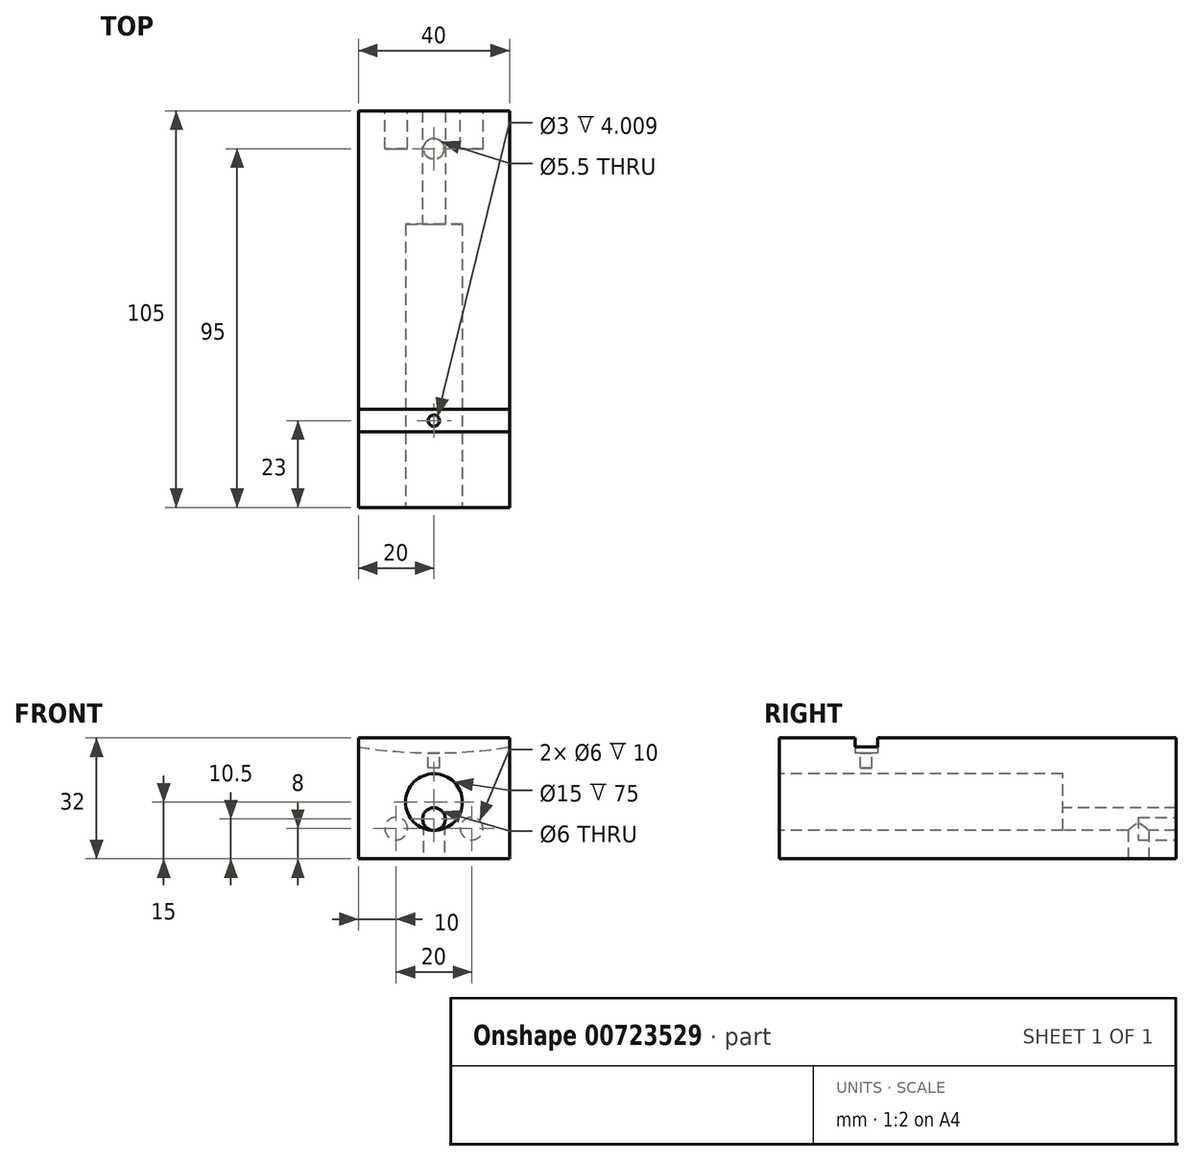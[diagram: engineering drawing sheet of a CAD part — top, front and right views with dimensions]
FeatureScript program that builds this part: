
annotation { "Feature Type Name" : "Feature", "Feature Type Description" : "" }
export const myFeature = defineFeature(function(context is Context, id is Id, definition is map)
    precondition{}
    {
        {
            var Q0;
            Q0=qCreatedBy(makeId("Front.planeOp"),FACE);
            var sketch = newSketch(context, id + "F0", { "sketchPlane" : qUnion([Q0])});
            skLineSegment(sketch, "E0.bottom", {"start": v(0, 0) * mm, "end": v(-40, 0) * mm});
            skLineSegment(sketch, "E0.top", {"start": v(0, 32) * mm, "end": v(-40, 32) * mm});
            skLineSegment(sketch, "E0.left", {"start": v(0, 0) * mm, "end": v(0, 32) * mm});
            skLineSegment(sketch, "E0.right", {"start": v(-40, 0) * mm, "end": v(-40, 32) * mm});
            skSolve(sketch);
        }
        {
            var Q0;
            Q0=qSketchRegion(id+"F0",true);
            extrude(context, id + "F1", {"entities" : qUnion([Q0]), "oppositeDirection" : true, "depth" : 105 * mm, "offsetDistance" : 25 * mm});
        }
        {
            var Q0;
            Q0=makeQuery(id+"F1.opExtrude","CAP_FACE",FACE,{"disambiguationData":[OSD([sQuery(id+"F0.wireOp",EDGE,"E0.bottom"),sQuery(id+"F0.wireOp",EDGE,"E0.top"),sQuery(id+"F0.wireOp",EDGE,"E0.left"),sQuery(id+"F0.wireOp",EDGE,"E0.right")])],"isStart":true});
            var sketch = newSketch(context, id + "F2", { "sketchPlane" : qUnion([Q0])});
            skPoint(sketch, "E1.centerSnap0", {"position": v(0, 16) * mm});
            skPoint(sketch, "E1.centerSnap1", {"position": v(-20, 0) * mm});
            skLineSegment(sketch, "E2", {"start": v(-20, 0) * mm, "end": v(-20, 15) * mm, "construction": true});
            skCircle(sketch, "E3", {"center": v(-20, 15) * mm, "radius": 7.5 * mm});
            skSolve(sketch);
        }
        {
            var Q0;
            Q0=qSketchRegion(id+"F2",true);
            extrude(context, id + "F3", {"entities" : qUnion([Q0]), "operationType" : NewBodyOperationType.REMOVE, "oppositeDirection" : true, "depth" : 75 * mm, "offsetDistance" : 25 * mm});
        }
        {
            var Q0;
            Q0=qCreatedBy(makeId("Front.planeOp"),FACE);
            var sketch = newSketch(context, id + "F4", { "sketchPlane" : qUnion([Q0])});
            skLineSegment(sketch, "E4", {"start": v(0, 0) * mm, "end": v(-20, 0) * mm, "construction": true});
            skLineSegment(sketch, "E5", {"start": v(-20, 0) * mm, "end": v(-20, 15) * mm, "construction": true});
            skLineSegment(sketch, "E6", {"start": v(-20, 15) * mm, "end": v(-20, 7.5) * mm, "construction": true});
            skLineSegment(sketch, "E7", {"start": v(-20, 7.5) * mm, "end": v(-20, 10.5) * mm, "construction": true});
            skCircle(sketch, "E8", {"center": v(-20, 10.5) * mm, "radius": 3 * mm});
            skSolve(sketch);
        }
        {
            var Q0;
            Q0=qSketchRegion(id+"F4",true);
            extrude(context, id + "F5", {"entities" : qUnion([Q0]), "operationType" : NewBodyOperationType.REMOVE, "endBound" : BoundingType.THROUGH_ALL, "oppositeDirection" : true, "depth" : 25 * mm, "offsetDistance" : 25 * mm});
        }
        {
            var Q0;
            Q0=qCreatedBy(makeId("Front.planeOp"),FACE);
            cPlane(context, id + "F6", {"entities" : qUnion([Q0]), "cplaneType" : CPlaneType.OFFSET, "offset" : 20 * mm, "oppositeDirection" : true, "width" : 150 * mm, "height" : 150 * mm});
        }
        {
            var Q0;
            Q0=qCreatedBy(id+"F6.planeOp",FACE);
            var sketch = newSketch(context, id + "F7", { "sketchPlane" : qUnion([Q0])});
            skLineSegment(sketch, "E9", {"start": v(0, 0) * mm, "end": v(0, 32) * mm, "construction": true});
            skLineSegment(sketch, "E10", {"start": v(0, 32) * mm, "end": v(-40, 32) * mm, "construction": true});
            skLineSegment(sketch, "E11", {"start": v(-40, 32) * mm, "end": v(-40, 28) * mm, "construction": true});
            skLineSegment(sketch, "E12", {"start": v(-40, 28) * mm, "end": v(0, 28) * mm, "construction": true});
            skLineSegment(sketch, "E13", {"start": v(-20, 28) * mm, "end": v(-20, 278) * mm, "construction": true});
            skCircle(sketch, "E14", {"center": v(-20, 153) * mm, "radius": 125 * mm});
            skLineSegment(sketch, "E15", {"start": v(0, 0) * mm, "end": v(-20, 0) * mm, "construction": true});
            skLineSegment(sketch, "E16", {"start": v(-20, 0) * mm, "end": v(-20, 22.5) * mm, "construction": true});
            skSolve(sketch);
        }
        {
            var Q0;
            Q0=qSketchRegion(id+"F7",true);
            extrude(context, id + "F8", {"entities" : qUnion([Q0]), "operationType" : NewBodyOperationType.REMOVE, "oppositeDirection" : true, "depth" : 6 * mm, "offsetDistance" : 25 * mm});
        }
        {
            var Q0;
            {var subQ2=sQuery(id+"F0.wireOp",EDGE,"E0.top");Q0=makeQuery(id+"F8.boolean.opBoolean","SPLIT",FACE,{"disambiguationData":[TD([makeQuery(id+"F8.opExtrude","CAP_FACE",FACE,{"disambiguationData":[OSD([sQuery(id+"F7.wireOp",EDGE,"E14")])],"isStart":false})])],"derivedFrom":makeQuery(id+"F1.opExtrude","SWEPT_FACE",FACE,{"disambiguationData":[OSD([subQ2])]})});}
            cPlane(context, id + "F9", {"entities" : qUnion([Q0]), "cplaneType" : CPlaneType.OFFSET, "offset" : 0 * mm, "width" : 150 * mm, "height" : 150 * mm});
        }
        {
            var Q0;
            Q0=qCreatedBy(id+"F9.planeOp",FACE);
            var sketch = newSketch(context, id + "F10", { "sketchPlane" : qUnion([Q0])});
            skLineSegment(sketch, "E17", {"start": v(0, 0) * mm, "end": v(0, 23) * mm, "construction": true});
            skLineSegment(sketch, "E18", {"start": v(0, 23) * mm, "end": v(-20, 23) * mm, "construction": true});
            skCircle(sketch, "E19", {"center": v(-20, 23) * mm, "radius": 1.5 * mm});
            skSolve(sketch);
        }
        {
            var Q0;
            Q0 = qSketchRegion(id + "F10", true);
            extrude(context, id + "F11", {"entities" : qUnion([Q0]), "operationType" : NewBodyOperationType.REMOVE, "oppositeDirection" : true, "depth" : 8 * mm, "offsetDistance" : 25 * mm});
        }
        {
            var Q0;
            Q0=makeQuery(id+"F1.opExtrude","CAP_FACE",FACE,{"disambiguationData":[OSD([sQuery(id+"F0.wireOp",EDGE,"E0.bottom"),sQuery(id+"F0.wireOp",EDGE,"E0.top"),sQuery(id+"F0.wireOp",EDGE,"E0.left"),sQuery(id+"F0.wireOp",EDGE,"E0.right")])],"isStart":false});
            cPlane(context, id + "F12", {"entities" : qUnion([Q0]), "cplaneType" : CPlaneType.OFFSET, "offset" : 0 * mm, "width" : 150 * mm, "height" : 150 * mm});
        }
        {
            var Q0;
            Q0=qCreatedBy(id+"F12.planeOp",FACE);
            var sketch = newSketch(context, id + "F13", { "sketchPlane" : qUnion([Q0])});
            skLineSegment(sketch, "E20", {"start": v(0, 0) * mm, "end": v(20, 0) * mm, "construction": true});
            skLineSegment(sketch, "E21", {"start": v(20, 0) * mm, "end": v(20, 240) * mm, "construction": true});
            skCircle(sketch, "E22", {"center": v(20, 120) * mm, "radius": 120 * mm, "construction": true});
            skLineSegment(sketch, "E23", {"start": v(0, 0) * mm, "end": v(10, 0) * mm});
            skLineSegment(sketch, "E24", {"start": v(10, 0) * mm, "end": v(10, 8) * mm, "construction": true});
            skCircle(sketch, "E25", {"center": v(10, 8) * mm, "radius": 3 * mm});
            skCircle(sketch, "E26.MirrorC", {"center": v(30, 8) * mm, "radius": 3 * mm});
            skSolve(sketch);
        }
        {
            var Q0;
            Q0 = qSketchRegion(id + "F13", true);
            extrude(context, id + "F14", {"entities" : qUnion([Q0]), "operationType" : NewBodyOperationType.REMOVE, "oppositeDirection" : true, "depth" : 10 * mm, "offsetDistance" : 25 * mm});
        }
        {
            var Q0;
            Q0=makeQuery(id+"F1.opExtrude","SWEPT_FACE",FACE,{"disambiguationData":[OSD([sQuery(id+"F0.wireOp",EDGE,"E0.bottom")])]});
            cPlane(context, id + "F15", {"entities" : qUnion([Q0]), "cplaneType" : CPlaneType.OFFSET, "offset" : 0 * mm, "width" : 150 * mm, "height" : 150 * mm});
        }
        {
            var Q0;
            Q0=qCreatedBy(id+"F15.planeOp",FACE);
            var sketch = newSketch(context, id + "F16", { "sketchPlane" : qUnion([Q0])});
            skLineSegment(sketch, "E27", {"start": v(0, 0) * mm, "end": v(0, -105) * mm, "construction": true});
            skLineSegment(sketch, "E28", {"start": v(0, -105) * mm, "end": v(-20, -105) * mm, "construction": true});
            skLineSegment(sketch, "E29", {"start": v(-20, -105) * mm, "end": v(-20, -95) * mm, "construction": true});
            skCircle(sketch, "E30", {"center": v(-20, -95) * mm, "radius": 2.75 * mm});
            skSolve(sketch);
        }
        {
            var Q0;
            Q0 = qSketchRegion(id + "F16", true);
            extrude(context, id + "F17", {"entities" : qUnion([Q0]), "operationType" : NewBodyOperationType.REMOVE, "oppositeDirection" : true, "depth" : 11.7 * mm, "offsetDistance" : 25 * mm});
        }
    });
